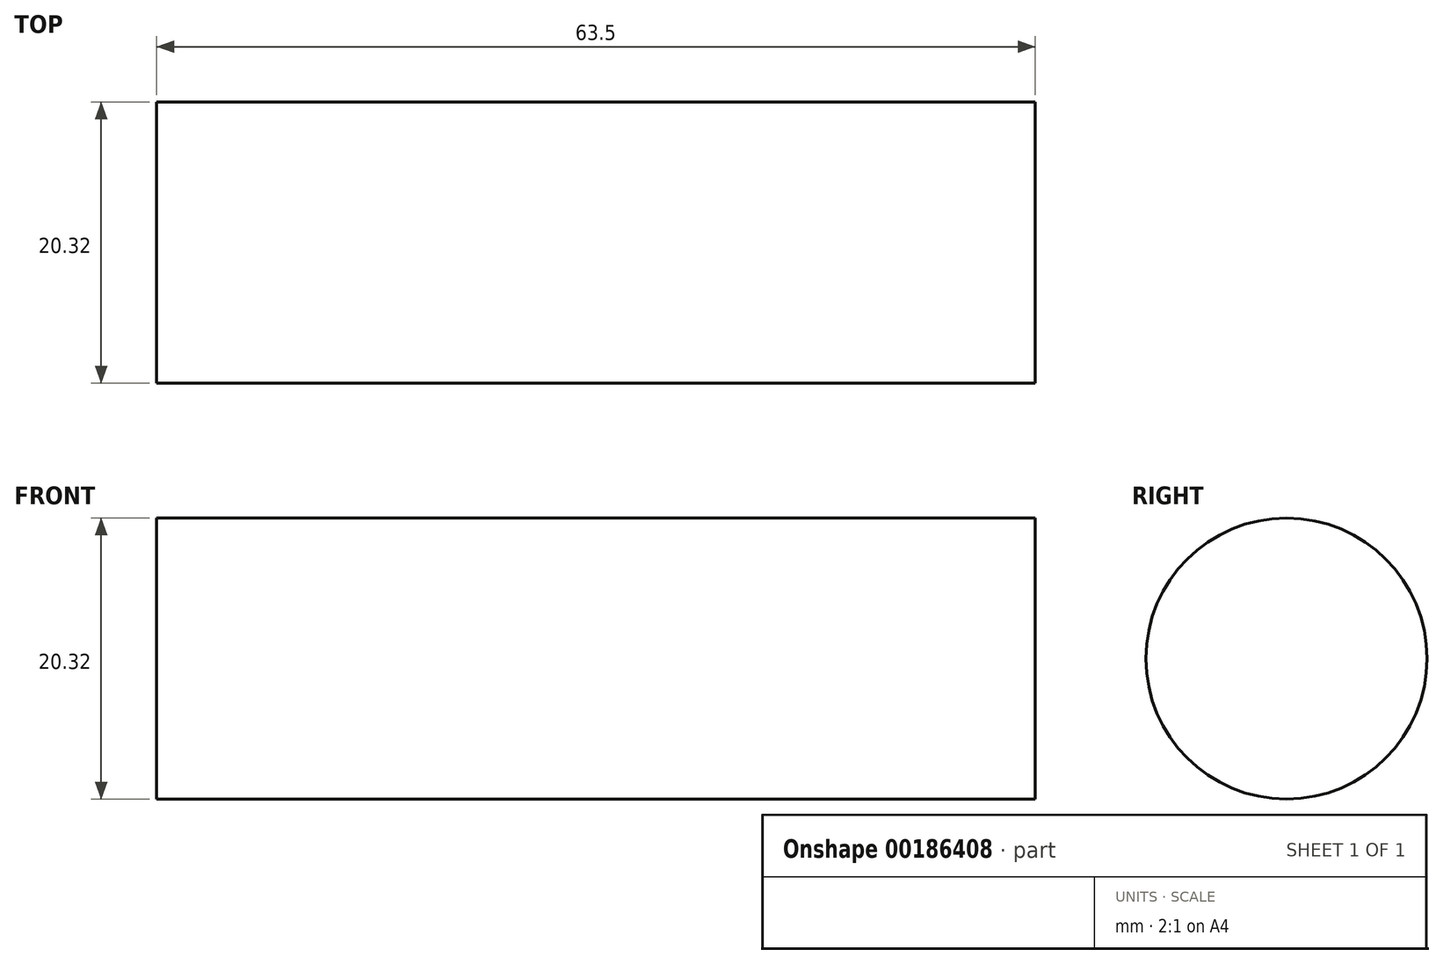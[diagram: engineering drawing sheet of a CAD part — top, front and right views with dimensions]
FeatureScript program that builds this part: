
annotation { "Feature Type Name" : "Feature", "Feature Type Description" : "" }
export const myFeature = defineFeature(function(context is Context, id is Id, definition is map)
    precondition{}
    {
        {
            var Q0;
            Q0=qCreatedBy(makeId("Right.planeOp"),FACE);
            var sketch = newSketch(context, id + "F0", { "sketchPlane" : qUnion([Q0])});
            skCircle(sketch, "E0", {"center": v(-38.7, 34.51) * mm, "radius": 10.16 * mm});
            skSolve(sketch);
        }
        {
            var Q0;
            Q0=makeQuery(id+"F0.imprint","IMPRINT",FACE,{"disambiguationData":[TD([[makeQuery(id+"F0.imprint","IMPRINT",EDGE,{"derivedFrom":sQuery(id+"F0.wireOp",EDGE,"E0")}),1.0]])]});
            extrude(context, id + "F1", {"entities" : qUnion([Q0]), "depth" : 63.5 * mm});
        }
    });
